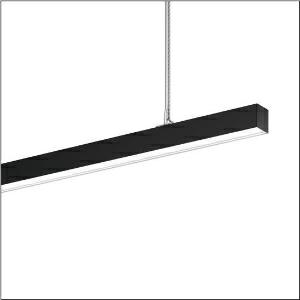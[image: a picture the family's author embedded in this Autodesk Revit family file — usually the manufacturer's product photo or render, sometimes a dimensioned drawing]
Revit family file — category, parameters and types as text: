
# Revit family: silica_r__21_51mx30da34bb_31c6
name_source: partatom
category: Lighting Fixtures
units: mm (PartAtom-declared; Revit-internal decimal feet)

## family parameters
Cut with Voids When Loaded = No
Host = Face
Light Source = No
Part Type = Normal
Room Calculation Point = No
Round Connector Dimension = Use Diameter
Shared = No

## types (1)
- --- (1 x LED, 4210 lm, 27.7 W, 3000K)
    Apparent Load = 28 VA
    CIE Flux Codes = 47 79 96 57 100
    Color Rendering = 80
    Color Temperature = 3000K
    Default Elevation = 1800 mm
    Description = Silica® 21, office luminaire, primary optical cover: cover, of PMMA, opal, light emission: direct/indirect distribution, primary light characteristic: symmetric, installation type: suspended mounting, LED, rated luminous flux: 4.210lm, luminous efficacy: 152lm/W, light colour: 830, colour temperature: 3000K, with terminal, 3+2-pole, max. 2.5mm², mains connection: 220..240V, AC, 50/60Hz, rated input power: 27.7W, luminaire housing, of aluminium, jet black (RAL 9005), length: 1.204mm, width: 53mm, height: 53mm, protection rating (complete): IP20, insulation class (complete): insulation class I (protective earthing), certification: CE, permissible operating ambient temperature: 0..+35°C, standard: EN 50419, packaging unit: 1 piece
    Height = 53 mm
    Lamp = 1 x LED
    Lamp Light Flux = 4210 lm
    Lamp Power = 27.7 W
    Lamp count = 1
    Length = 1204 mm
    Luminous efficacy = 152 lm/W
    Manufacturer = Siteco
    ModVariant = No
    Model = 51MX30DA34BB
    Mounting Place = Ceiling
    Mounting Type = Pendant
    Number of Poles = 1
    OnlyDefault = Yes
    Power Factor = 1
    Product Name = Silica® 21
    Product group = office luminaire | ceiling pendant
    ProductGroupID = 902
    Protection Class = Protection class I
    Protection Degree = IP 20
    RLX_Detail_Level = 1
    RLX_Emergency_Light_Flux = 0 lm
    RLX_Emergency_Type = 0
    RLX_Emergency_Type_DB = No
    RlxData = <blob elided: 25897 chars, md5=af6164bf>
    Socket = socket
    Standby Power = 0 W
    System Light Flux = 4210 lm
    System Power = 28 W
    Type Comments = factory setting: luminous flux: 100 % | dim-lin: 254 | 233 mA
    Type Image = l_1335856.jpg
    URL = http://relux.com
    VarID = @adj_086157
    Voltage = 0 V
    Weight = 0.00 kg
    Width = 53 mm

## geometry (parser evidence)
native form markers: Blend x4, Sweep x15
no freeform markers — native parametric forms only
